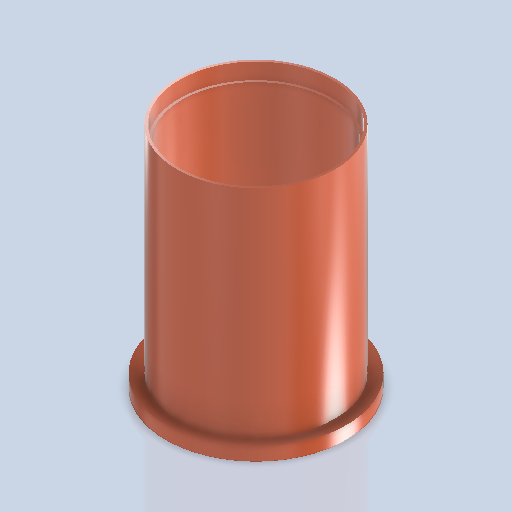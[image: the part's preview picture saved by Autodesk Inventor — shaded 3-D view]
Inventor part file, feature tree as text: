
AUTODESK INVENTOR PART (.ipt)
format: ipt  version: 2024.2 (Build 282272000, 272)  size: 253,952 bytes
history: native  units: mm
features: sketch x2, revolve x1, hole x1
ambient origin geometry x8: Origin, YZ Plane, XZ Plane, XY Plane, X Axis, Y Axis, Z Axis, Center Point
bodies: Volumenkörper1 (feature_tree)
feature tree (4):
  revolve  "Umdrehung1"
  hole  "Bohrung1"  [1 undecoded]
  sketch  "Skizze1"  dims[d0=112.0mm d1=8.0mm]
  sketch  "Skizze2"  dims[d2=134.0mm d3=98.0mm d4=90.0deg d5=92.0mm d6=50.0mm d7=95.0mm d8=10.0mm d9=90.0deg d10=50.0mm d11=0.0mm]
note: 1 required parameter value undecoded (feature->parameter linkage not recoverable at this tier; creation-order binding heuristic only, values carry confidence <= 0.55)
